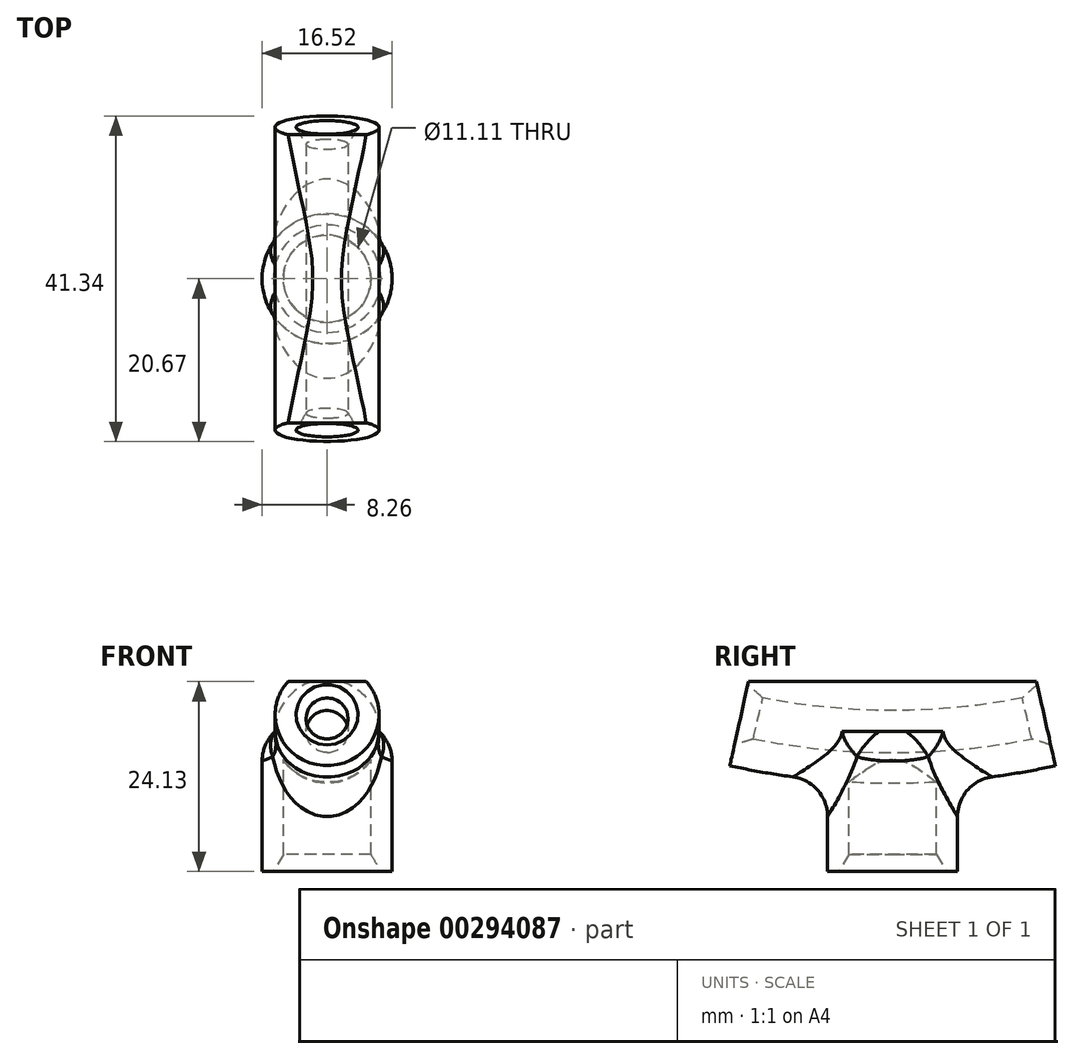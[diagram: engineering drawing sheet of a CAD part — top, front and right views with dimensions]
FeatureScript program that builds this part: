
annotation { "Feature Type Name" : "Feature", "Feature Type Description" : "" }
export const myFeature = defineFeature(function(context is Context, id is Id, definition is map)
    precondition{}
    {
        {
            var Q0;
            Q0=qCreatedBy(makeId("Front.planeOp"),FACE);
            var sketch = newSketch(context, id + "F0", { "sketchPlane" : qUnion([Q0])});
            skCircle(sketch, "E0", {"center": v(0, 0) * mm, "radius": 6.6 * mm});
            skLineSegment(sketch, "E1", {"start": v(-39.44, 88.9) * mm, "end": v(34.89, 88.9) * mm, "construction": true});
            skSolve(sketch);
        }
        {
            var Q0;
            Q0 = qSketchRegion(id + "F0", true);
            var Q1;
            Q1=sQuery(id+"F0.wireOp",EDGE,"E1");
            revolve(context, id + "F1", {"entities" : qUnion([Q0]), "axis" : qUnion([Q1]), "revolveType" : RevolveType.TWO_DIRECTIONS, "angle" : 12.5 * degree, "angleBack" : 347.5 * degree});
        }
        {
            var Q0;
            Q0=qCreatedBy(makeId("Top.planeOp"),FACE);
            var sketch = newSketch(context, id + "F2", { "sketchPlane" : qUnion([Q0])});
            skCircle(sketch, "E2", {"center": v(0, 0) * mm, "radius": 8.26 * mm});
            skCircle(sketch, "E3", {"center": v(0, 0) * mm, "radius": 5.56 * mm});
            skSolve(sketch);
        }
        {
            var Q0;
            Q0 = qSketchRegion(id + "F2", true);
            extrude(context, id + "F3", {"entities" : qUnion([Q0]), "operationType" : NewBodyOperationType.ADD, "oppositeDirection" : true, "depth" : 17.78 * mm});
        }
        {
            var Q0;
            Q0=makeQuery(id+"F3.boolean.opBoolean","INTERSECT",EDGE,{"disambiguationData":[OD(1.0)],"derivedFrom":[makeQuery(id+"F1.opRevolve","SWEPT_FACE",FACE,{"disambiguationData":[OSD([sQuery(id+"F0.wireOp",EDGE,"E0")])]}),makeQuery(id+"F3.opExtrude","SWEPT_FACE",FACE,{"disambiguationData":[OSD([sQuery(id+"F2.wireOp",EDGE,"E2")])]})]});
            var Q1;
            Q1=makeQuery(id+"F3.boolean.opBoolean","INTERSECT",EDGE,{"disambiguationData":[OD(0.0)],"derivedFrom":[makeQuery(id+"F1.opRevolve","SWEPT_FACE",FACE,{"disambiguationData":[OSD([sQuery(id+"F0.wireOp",EDGE,"E0")])]}),makeQuery(id+"F3.opExtrude","SWEPT_FACE",FACE,{"disambiguationData":[OSD([sQuery(id+"F2.wireOp",EDGE,"E2")])]})]});
            fillet(context, id + "F4", {"entities" : qUnion([Q0, Q1]), "radius" : 5.08 * mm, "tangentPropagation" : true, "allowEdgeOverflow" : false});
        }
        {
            var Q0;
            {var subQ0=sQuery(id+"F2.wireOp",EDGE,"E2");Q0=makeQuery(id+"F3.boolean.opBoolean","SPLIT",EDGE,{"disambiguationData":[TD([makeQuery(id+"F1.opRevolve","SWEPT_FACE",FACE,{"disambiguationData":[OSD([sQuery(id+"F0.wireOp",EDGE,"E0")])]}),makeQuery(id+"F3.opExtrude","SWEPT_FACE",FACE,{"disambiguationData":[OSD([subQ0])]}),makeQuery(id+"F3.opExtrude","CAP_FACE",FACE,{"disambiguationData":[OSD([subQ0,sQuery(id+"F2.wireOp",EDGE,"E3")])],"isStart":true})]),OD(1.0)],"derivedFrom":makeQuery(id+"F3.opExtrude","CAP_EDGE",EDGE,{"disambiguationData":[OSD([subQ0])],"isStart":true})});}
            var Q1;
            {var subQ0=sQuery(id+"F2.wireOp",EDGE,"E2");Q1=makeQuery(id+"F3.boolean.opBoolean","SPLIT",EDGE,{"disambiguationData":[TD([makeQuery(id+"F1.opRevolve","SWEPT_FACE",FACE,{"disambiguationData":[OSD([sQuery(id+"F0.wireOp",EDGE,"E0")])]}),makeQuery(id+"F3.opExtrude","SWEPT_FACE",FACE,{"disambiguationData":[OSD([subQ0])]}),makeQuery(id+"F3.opExtrude","CAP_FACE",FACE,{"disambiguationData":[OSD([subQ0,sQuery(id+"F2.wireOp",EDGE,"E3")])],"isStart":true})]),OD(0.0)],"derivedFrom":makeQuery(id+"F3.opExtrude","CAP_EDGE",EDGE,{"disambiguationData":[OSD([subQ0])],"isStart":true})});}
            fillet(context, id + "F5", {"entities" : qUnion([Q0, Q1]), "radius" : 5.08 * mm, "tangentPropagation" : true, "allowEdgeOverflow" : false});
        }
        {
            var Q0;
            Q0=qCreatedBy(makeId("Right.planeOp"),FACE);
            var sketch = newSketch(context, id + "F6", { "sketchPlane" : qUnion([Q0])});
            skLineSegment(sketch, "E4.bottom", {"start": v(-25.37, 16.58) * mm, "end": v(36.37, 16.58) * mm});
            skLineSegment(sketch, "E4.top", {"start": v(-25.37, 6.35) * mm, "end": v(36.37, 6.35) * mm});
            skLineSegment(sketch, "E4.left", {"start": v(-25.37, 16.58) * mm, "end": v(-25.37, 6.35) * mm});
            skLineSegment(sketch, "E4.right", {"start": v(36.37, 16.58) * mm, "end": v(36.37, 6.35) * mm});
            skSolve(sketch);
        }
        {
            var Q0;
            Q0=makeQuery(id+"F6.imprint","IMPRINT",FACE,{"disambiguationData":[TD([[makeQuery(id+"F6.imprint","IMPRINT",EDGE,{"derivedFrom":sQuery(id+"F6.wireOp",EDGE,"E4.bottom")}),-1.0]])]});
            extrude(context, id + "F7", {"entities" : qUnion([Q0]), "operationType" : NewBodyOperationType.REMOVE, "oppositeDirection" : true, "depth" : 25.4 * mm, "hasSecondDirection" : true, "secondDirectionOppositeDirection" : false, "secondDirectionDepth" : 25.4 * mm});
        }
        {
            var Q0;
            Q0=qCreatedBy(makeId("Front.planeOp"),FACE);
            var sketch = newSketch(context, id + "F8", { "sketchPlane" : qUnion([Q0])});
            skCircle(sketch, "E5", {"center": v(0, 0) * mm, "radius": 2.67 * mm});
            skLineSegment(sketch, "E6", {"start": v(-30.34, 88.9) * mm, "end": v(32.23, 88.9) * mm, "construction": true});
            skSolve(sketch);
        }
        {
            var Q0;
            Q0 = qSketchRegion(id + "F8", true);
            var Q1;
            Q1=sQuery(id+"F8.wireOp",EDGE,"E6");
            revolve(context, id + "F9", {"operationType" : NewBodyOperationType.REMOVE, "entities" : qUnion([Q0]), "axis" : qUnion([Q1]), "revolveType" : RevolveType.FULL, "oppositeDirection" : true});
        }
        {
            var Q0;
            Q0=makeQuery(id+"F3.opExtrude","CAP_EDGE",EDGE,{"disambiguationData":[OSD([sQuery(id+"F2.wireOp",EDGE,"E3")])],"isStart":false});
            chamfer(context, id + "F10", {"entities" : qUnion([Q0]), "chamferType" : ChamferType.OFFSET_ANGLE, "width" : 1.27 * mm, "oppositeDirection" : false, "angle" : 60 * degree, "tangentPropagation" : true});
        }
        {
            var Q0;
            Q0=makeQuery(id+"F9.boolean.opBoolean","INTERSECT",EDGE,{"derivedFrom":[makeQuery(id+"F1.opRevolve","CAP_FACE",FACE,{"disambiguationData":[OSD([sQuery(id+"F0.wireOp",EDGE,"E0")])],"isStart":true}),makeQuery(id+"F9.opRevolve","SWEPT_FACE",FACE,{"disambiguationData":[OSD([sQuery(id+"F8.wireOp",EDGE,"E5")])]})]});
            var Q1;
            Q1=makeQuery(id+"F9.boolean.opBoolean","INTERSECT",EDGE,{"derivedFrom":[makeQuery(id+"F1.opRevolve","CAP_FACE",FACE,{"disambiguationData":[OSD([sQuery(id+"F0.wireOp",EDGE,"E0")])],"isStart":false}),makeQuery(id+"F9.opRevolve","SWEPT_FACE",FACE,{"disambiguationData":[OSD([sQuery(id+"F8.wireOp",EDGE,"E5")])]})]});
            chamfer(context, id + "F11", {"entities" : qUnion([Q0, Q1]), "chamferType" : ChamferType.OFFSET_ANGLE, "width" : 1.27 * mm, "oppositeDirection" : false, "angle" : 60 * degree, "tangentPropagation" : true});
        }
    });
